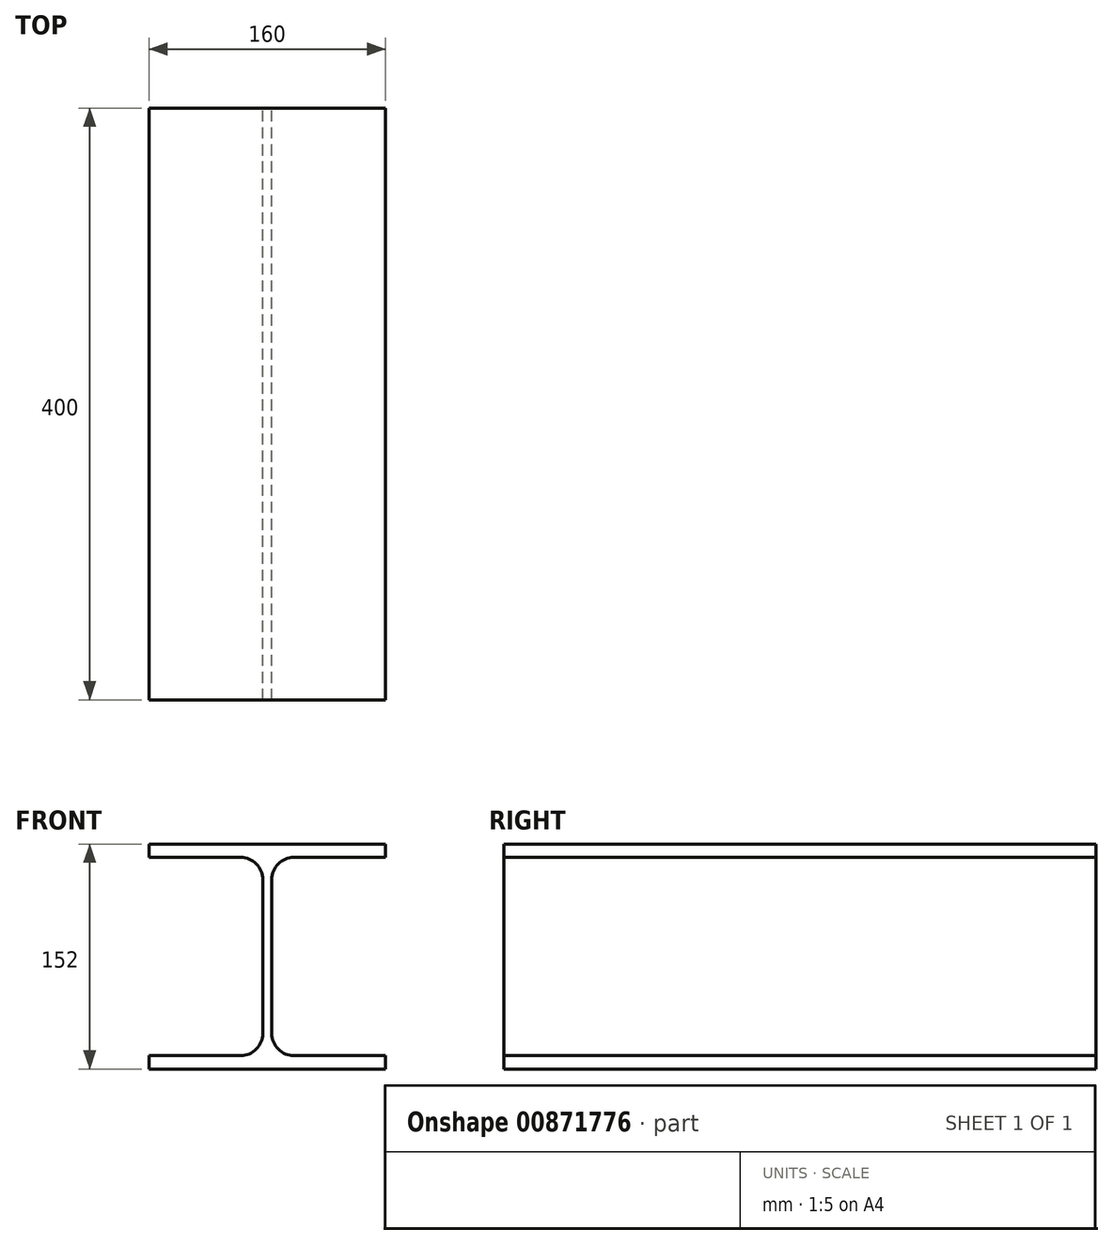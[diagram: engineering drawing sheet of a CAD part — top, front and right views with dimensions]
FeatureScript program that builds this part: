
annotation { "Feature Type Name" : "Feature", "Feature Type Description" : "" }
export const myFeature = defineFeature(function(context is Context, id is Id, definition is map)
    precondition{}
    {
        {
            var Q0;
            Q0=qCreatedBy(makeId("Front.planeOp"),FACE);
            var sketch = newSketch(context, id + "F0", { "sketchPlane" : qUnion([Q0])});
            skLineSegment(sketch, "E0.bottom", {"start": v(-97.55, -68.95) * mm, "end": v(-35.55, -68.95) * mm});
            skLineSegment(sketch, "E0.top", {"start": v(-97.55, -77.95) * mm, "end": v(62.45, -77.95) * mm});
            skLineSegment(sketch, "E0.left", {"start": v(-97.55, -68.95) * mm, "end": v(-97.55, -77.95) * mm});
            skLineSegment(sketch, "E0.right", {"start": v(62.45, -68.95) * mm, "end": v(62.45, -77.95) * mm});
            skLineSegment(sketch, "E1.bottom", {"start": v(-17.55, -68.95) * mm, "end": v(-14.55, -68.95) * mm});
            skLineSegment(sketch, "E1.top", {"start": v(-17.55, 65.05) * mm, "end": v(-14.55, 65.05) * mm});
            skLineSegment(sketch, "E1.left", {"start": v(-17.55, -68.95) * mm, "end": v(-17.55, 65.05) * mm});
            skLineSegment(sketch, "E1.right", {"start": v(-14.55, -53.95) * mm, "end": v(-14.55, 50.05) * mm});
            skLineSegment(sketch, "E2.bottom", {"start": v(-17.55, -68.95) * mm, "end": v(-20.55, -68.95) * mm});
            skLineSegment(sketch, "E2.top", {"start": v(-17.55, 65.05) * mm, "end": v(-20.55, 65.05) * mm});
            skLineSegment(sketch, "E2.right", {"start": v(-20.55, -53.95) * mm, "end": v(-20.55, 50.05) * mm});
            skLineSegment(sketch, "E3.bottom", {"start": v(-97.55, 65.05) * mm, "end": v(-35.55, 65.05) * mm});
            skLineSegment(sketch, "E3.top", {"start": v(-97.55, 74.05) * mm, "end": v(62.45, 74.05) * mm});
            skLineSegment(sketch, "E3.left", {"start": v(-97.55, 65.05) * mm, "end": v(-97.55, 74.05) * mm});
            skLineSegment(sketch, "E3.right", {"start": v(62.45, 65.05) * mm, "end": v(62.45, 74.05) * mm});
            skArc(sketch, "E4.filletArc", {"start": v(-20.55, 50.05) * mm, "mid": v(-24.95, 60.66) * mm, "end": v(-35.55, 65.05) * mm});
            skPoint(sketch, "E5.newPointA", {"position": v(62.45, -68.95) * mm});
            skArc(sketch, "E5.filletArc", {"start": v(-35.55, -68.95) * mm, "mid": v(-24.95, -64.55) * mm, "end": v(-20.55, -53.95) * mm});
            skLineSegment(sketch, "E6", {"start": v(0.45, -68.95) * mm, "end": v(62.45, -68.95) * mm});
            skLineSegment(sketch, "E7", {"start": v(0.45, 65.05) * mm, "end": v(62.45, 65.05) * mm});
            skPoint(sketch, "E8.visualSharp", {"position": v(-14.55, 65.05) * mm});
            skArc(sketch, "E8.filletArc", {"start": v(0.45, 65.05) * mm, "mid": v(-10.16, 60.66) * mm, "end": v(-14.55, 50.05) * mm});
            skPoint(sketch, "E9.visualSharp", {"position": v(-14.55, -68.95) * mm});
            skArc(sketch, "E9.filletArc", {"start": v(-14.55, -53.95) * mm, "mid": v(-10.16, -64.55) * mm, "end": v(0.45, -68.95) * mm});
            skSolve(sketch);
        }
        {
            var Q0;
            Q0 = qSketchRegion(id + "F0", true);
            extrude(context, id + "F1", {"entities" : qUnion([Q0]), "depth" : 400 * mm, "offsetDistance" : 25 * mm});
        }
    });
